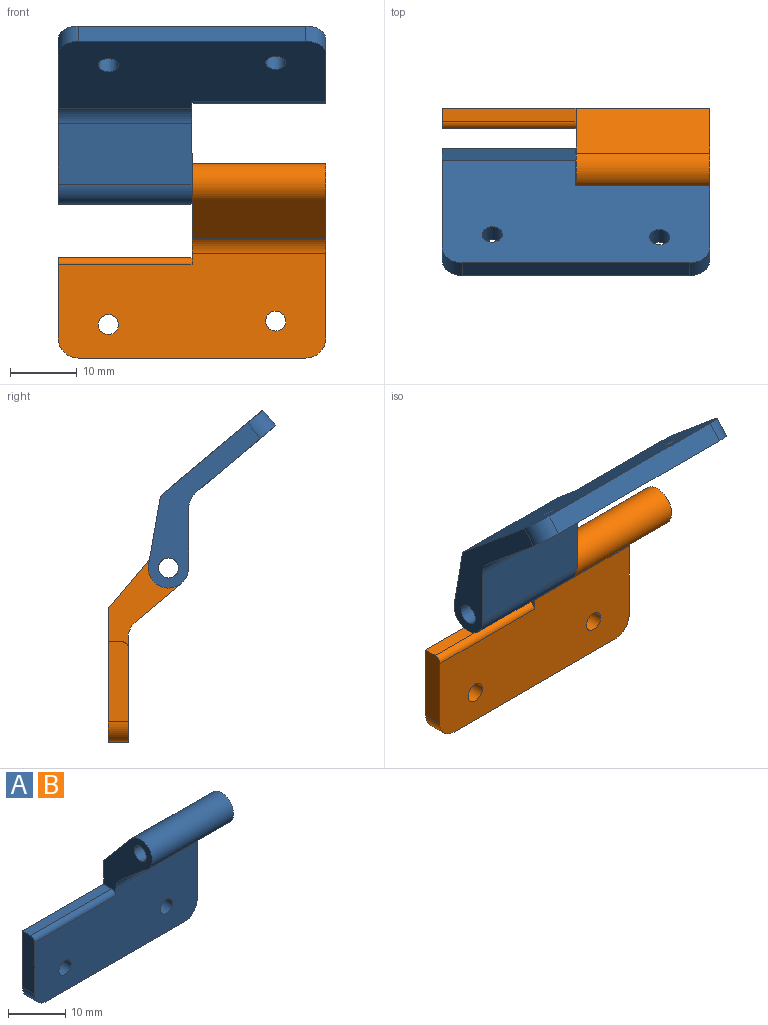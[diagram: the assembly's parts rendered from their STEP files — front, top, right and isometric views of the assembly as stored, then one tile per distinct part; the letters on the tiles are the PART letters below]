
ASSEMBLY  parts=2 mates=1
PART A: 17 faces, bbox 40x12x29 mm
  f0: plane 12x3mm, normal (-1,0,0), area 35.8mm2, adj f2,f4,f5,f12,f15
  f1: plane 34x3mm, normal (0,0,-1), area 102mm2, adj f4,f5,f14,f15
  f2: plane 20x2mm, normal (0,0,1), area 40mm2, adj f0,f5,f11,f12
  f3: cylinder r=1.5mm len=3mm, axis (0,1,0), area 28.3mm2, adj f4,f5
  f4: plane 40x15.61mm, normal (0,-1,0), area 574.2mm2, adj f0,f1,f3,f10,f11,f12,f13,f14
  f5: plane 40x20mm, normal (0,1,0), area 682mm2, adj f0,f1,f2,f3,f6,f10,f11,f14
  f6: plane 20x7.94mm, normal (0,0.76,0.65), area 207.8mm2, adj f5,f7,f10,f11
  f7: cylinder r=3mm len=20mm, axis (-1,0,0), area 198.5mm2, adj f6,f8,f10,f11
  f8: plane 20x6.87mm, normal (0,-0.65,-0.76), area 180mm2, adj f7,f10,f11,f13
  f9: cylinder r=1.5mm len=20mm, axis (-1,0,0), area 188.5mm2, adj f10,f11
  f10: plane 26x12mm, normal (1,0,0), area 108.3mm2, adj f4,f5,f6,f7,f8,f9,f13,f14
  f11: plane 15x12mm, normal (-1,0,0), area 72.5mm2, adj f2,f4,f5,f6,f7,f8,f9,f12
  f12: cylinder r=1mm len=20mm, axis (1,0,0), area 31.4mm2, adj f0,f2,f4,f11
  f13: cylinder r=3mm len=20mm, axis (1,0,0), area 52.1mm2, adj f4,f8,f10,f11
  f14: cylinder r=3mm len=3mm, axis (0,-1,0), area 14.1mm2, adj f1,f4,f5,f10
  f15: cylinder r=3mm len=3mm, axis (0,-1,0), area 14.1mm2, adj f0,f1,f4,f5
  f16: cylinder r=1.5mm len=3mm, axis (0,-1,0), area 28.3mm2, adj f4,f5
PART B: same geometry as A
PLACE A rot(axis=(0,0.91,0.42),180deg) t=(0,-20.13,46.61)mm
PLACE B t=(-40,3,-3)mm
MATE revolute B.f7 <-> A.f7  axis (-1,0,0) through (-20,-6,23)mm
